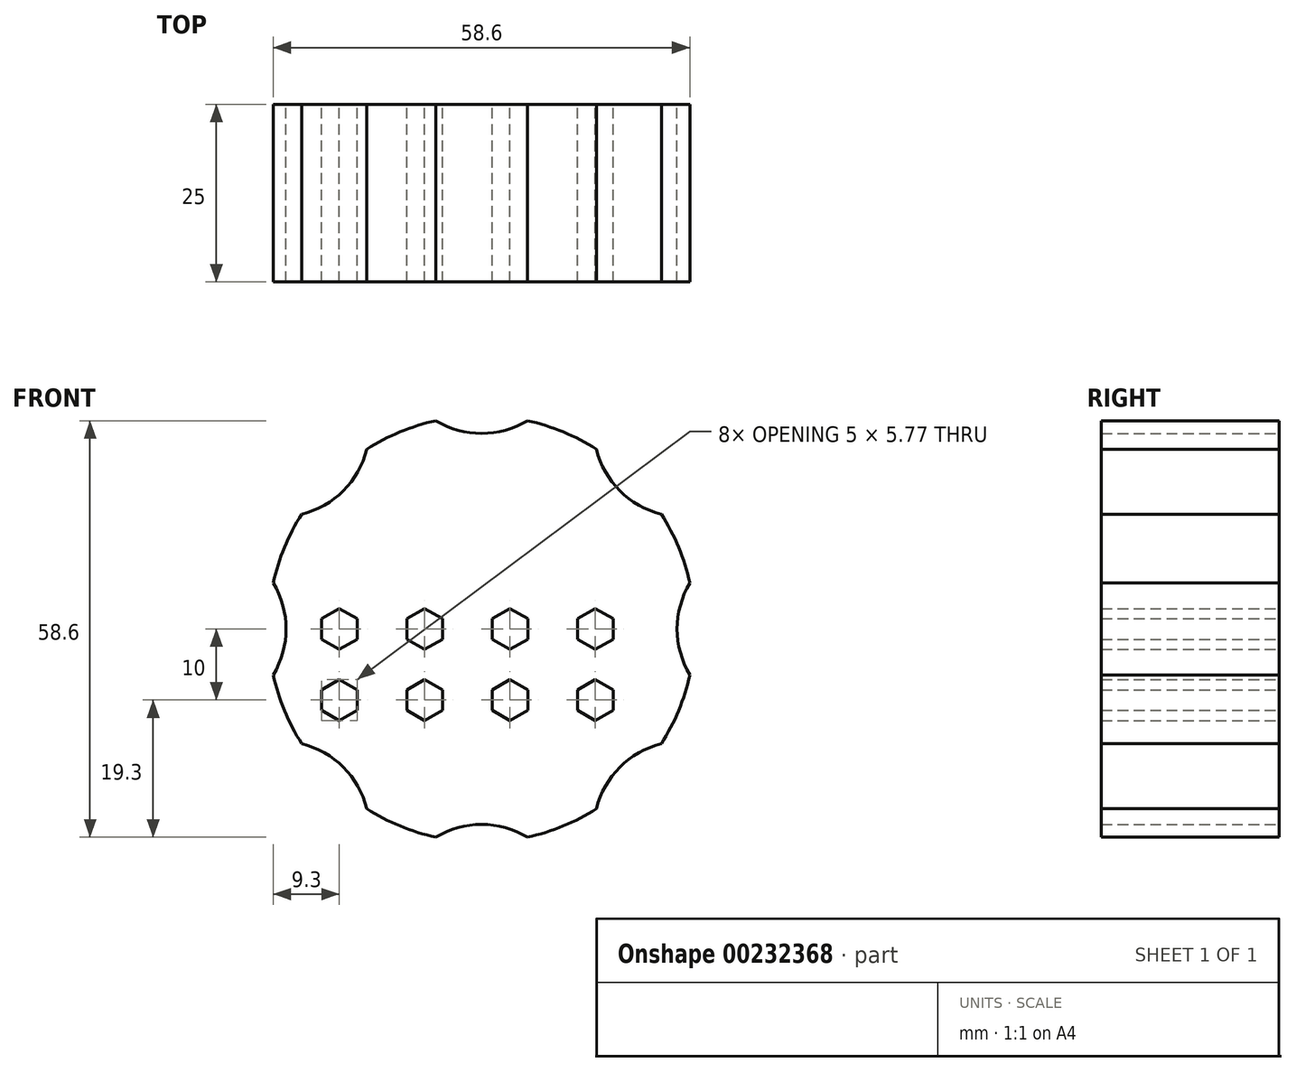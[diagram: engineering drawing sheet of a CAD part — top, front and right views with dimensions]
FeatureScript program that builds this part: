
annotation { "Feature Type Name" : "Feature", "Feature Type Description" : "" }
export const myFeature = defineFeature(function(context is Context, id is Id, definition is map)
    precondition{}
    {
        {
            var Q0;
            Q0=qCreatedBy(makeId("Front.planeOp"),FACE);
            var sketch = newSketch(context, id + "F0", { "sketchPlane" : qUnion([Q0])});
            skArc(sketch, "E0", {"start": v(29.3, 6.46) * mm, "mid": v(27.72, 11.48) * mm, "end": v(25.28, 16.15) * mm});
            skLineSegment(sketch, "E1", {"start": v(-41.86, -10) * mm, "end": v(18.85, -10) * mm, "construction": true});
            skLineSegment(sketch, "E2", {"start": v(-20, -35.68) * mm, "end": v(-20, 9.52) * mm, "construction": true});
            skLineSegment(sketch, "E3", {"start": v(-42.7, 5) * mm, "end": v(18.85, 5) * mm, "construction": true});
            skCircle(sketch, "E4.cCircle", {"center": v(-20, -10) * mm, "radius": 2.5 * mm, "construction": true});
            skLineSegment(sketch, "E4.0", {"start": v(-17.5, -11.44) * mm, "end": v(-20, -12.89) * mm});
            skLineSegment(sketch, "E4.1", {"start": v(-20, -12.89) * mm, "end": v(-22.5, -11.44) * mm});
            skLineSegment(sketch, "E4.2", {"start": v(-22.5, -11.44) * mm, "end": v(-22.5, -8.56) * mm});
            skLineSegment(sketch, "E4.3", {"start": v(-22.5, -8.56) * mm, "end": v(-20, -7.11) * mm});
            skLineSegment(sketch, "E4.4", {"start": v(-20, -7.11) * mm, "end": v(-17.5, -8.56) * mm});
            skLineSegment(sketch, "E4.5", {"start": v(-17.5, -8.56) * mm, "end": v(-17.5, -11.44) * mm});
            skPoint(sketch, "E4.0.midPoint", {"position": v(-18.75, -12.17) * mm});
            skLineSegment(sketch, "E5", {"start": v(40, 21.36) * mm, "end": v(40, -23.63) * mm, "construction": true});
            skArc(sketch, "E6", {"start": v(29.3, 6.46) * mm, "mid": v(27.5, 0) * mm, "end": v(29.3, -6.46) * mm});
            skLineSegment(sketch, "E7.0.1.0", {"start": v(-17.5, -1.44) * mm, "end": v(-20, -2.89) * mm});
            skLineSegment(sketch, "E7.0.1.1", {"start": v(-17.5, 1.44) * mm, "end": v(-17.5, -1.44) * mm});
            skCircle(sketch, "E7.0.1.2", {"center": v(-20, 0) * mm, "radius": 2.5 * mm, "construction": true});
            skLineSegment(sketch, "E7.0.1.3", {"start": v(-20, 2.89) * mm, "end": v(-17.5, 1.44) * mm});
            skLineSegment(sketch, "E7.0.1.4", {"start": v(-22.5, 1.44) * mm, "end": v(-20, 2.89) * mm});
            skLineSegment(sketch, "E7.0.1.5", {"start": v(-22.5, -1.44) * mm, "end": v(-22.5, 1.44) * mm});
            skLineSegment(sketch, "E7.0.1.6", {"start": v(-20, -2.89) * mm, "end": v(-22.5, -1.44) * mm});
            skLineSegment(sketch, "E7.1.0.0", {"start": v(-5.5, -11.44) * mm, "end": v(-8, -12.89) * mm});
            skLineSegment(sketch, "E7.1.0.1", {"start": v(-5.5, -8.56) * mm, "end": v(-5.5, -11.44) * mm});
            skCircle(sketch, "E7.1.0.2", {"center": v(-8, -10) * mm, "radius": 2.5 * mm, "construction": true});
            skLineSegment(sketch, "E7.1.0.3", {"start": v(-8, -7.11) * mm, "end": v(-5.5, -8.56) * mm});
            skLineSegment(sketch, "E7.1.0.4", {"start": v(-10.5, -8.56) * mm, "end": v(-8, -7.11) * mm});
            skLineSegment(sketch, "E7.1.0.5", {"start": v(-10.5, -11.44) * mm, "end": v(-10.5, -8.56) * mm});
            skLineSegment(sketch, "E7.1.0.6", {"start": v(-8, -12.89) * mm, "end": v(-10.5, -11.44) * mm});
            skLineSegment(sketch, "E7.1.1.0", {"start": v(-5.5, -1.44) * mm, "end": v(-8, -2.89) * mm});
            skLineSegment(sketch, "E7.1.1.1", {"start": v(-5.5, 1.44) * mm, "end": v(-5.5, -1.44) * mm});
            skCircle(sketch, "E7.1.1.2", {"center": v(-8, 0) * mm, "radius": 2.5 * mm, "construction": true});
            skLineSegment(sketch, "E7.1.1.3", {"start": v(-8, 2.89) * mm, "end": v(-5.5, 1.44) * mm});
            skLineSegment(sketch, "E7.1.1.4", {"start": v(-10.5, 1.44) * mm, "end": v(-8, 2.89) * mm});
            skLineSegment(sketch, "E7.1.1.5", {"start": v(-10.5, -1.44) * mm, "end": v(-10.5, 1.44) * mm});
            skLineSegment(sketch, "E7.1.1.6", {"start": v(-8, -2.89) * mm, "end": v(-10.5, -1.44) * mm});
            skLineSegment(sketch, "E7.2.0.0", {"start": v(6.5, -11.44) * mm, "end": v(4, -12.89) * mm});
            skLineSegment(sketch, "E7.2.0.1", {"start": v(6.5, -8.56) * mm, "end": v(6.5, -11.44) * mm});
            skCircle(sketch, "E7.2.0.2", {"center": v(4, -10) * mm, "radius": 2.5 * mm, "construction": true});
            skLineSegment(sketch, "E7.2.0.3", {"start": v(4, -7.11) * mm, "end": v(6.5, -8.56) * mm});
            skLineSegment(sketch, "E7.2.0.4", {"start": v(1.5, -8.56) * mm, "end": v(4, -7.11) * mm});
            skLineSegment(sketch, "E7.2.0.5", {"start": v(1.5, -11.44) * mm, "end": v(1.5, -8.56) * mm});
            skLineSegment(sketch, "E7.2.0.6", {"start": v(4, -12.89) * mm, "end": v(1.5, -11.44) * mm});
            skLineSegment(sketch, "E7.2.1.0", {"start": v(6.5, -1.44) * mm, "end": v(4, -2.89) * mm});
            skLineSegment(sketch, "E7.2.1.1", {"start": v(6.5, 1.44) * mm, "end": v(6.5, -1.44) * mm});
            skCircle(sketch, "E7.2.1.2", {"center": v(4, 0) * mm, "radius": 2.5 * mm, "construction": true});
            skLineSegment(sketch, "E7.2.1.3", {"start": v(4, 2.89) * mm, "end": v(6.5, 1.44) * mm});
            skLineSegment(sketch, "E7.2.1.4", {"start": v(1.5, 1.44) * mm, "end": v(4, 2.89) * mm});
            skLineSegment(sketch, "E7.2.1.5", {"start": v(1.5, -1.44) * mm, "end": v(1.5, 1.44) * mm});
            skLineSegment(sketch, "E7.2.1.6", {"start": v(4, -2.89) * mm, "end": v(1.5, -1.44) * mm});
            skLineSegment(sketch, "E7.3.0.0", {"start": v(18.5, -11.44) * mm, "end": v(16, -12.89) * mm});
            skLineSegment(sketch, "E7.3.0.1", {"start": v(18.5, -8.56) * mm, "end": v(18.5, -11.44) * mm});
            skCircle(sketch, "E7.3.0.2", {"center": v(16, -10) * mm, "radius": 2.5 * mm, "construction": true});
            skLineSegment(sketch, "E7.3.0.3", {"start": v(16, -7.11) * mm, "end": v(18.5, -8.56) * mm});
            skLineSegment(sketch, "E7.3.0.4", {"start": v(13.5, -8.56) * mm, "end": v(16, -7.11) * mm});
            skLineSegment(sketch, "E7.3.0.5", {"start": v(13.5, -11.44) * mm, "end": v(13.5, -8.56) * mm});
            skLineSegment(sketch, "E7.3.0.6", {"start": v(16, -12.89) * mm, "end": v(13.5, -11.44) * mm});
            skLineSegment(sketch, "E7.3.1.0", {"start": v(18.5, -1.44) * mm, "end": v(16, -2.89) * mm});
            skLineSegment(sketch, "E7.3.1.1", {"start": v(18.5, 1.44) * mm, "end": v(18.5, -1.44) * mm});
            skCircle(sketch, "E7.3.1.2", {"center": v(16, 0) * mm, "radius": 2.5 * mm, "construction": true});
            skLineSegment(sketch, "E7.3.1.3", {"start": v(16, 2.89) * mm, "end": v(18.5, 1.44) * mm});
            skLineSegment(sketch, "E7.3.1.4", {"start": v(13.5, 1.44) * mm, "end": v(16, 2.89) * mm});
            skLineSegment(sketch, "E7.3.1.5", {"start": v(13.5, -1.44) * mm, "end": v(13.5, 1.44) * mm});
            skLineSegment(sketch, "E7.3.1.6", {"start": v(16, -2.89) * mm, "end": v(13.5, -1.44) * mm});
            skLineSegment(sketch, "E7.direction1", {"start": v(-20, -12.89) * mm, "end": v(-8, -12.89) * mm, "construction": true});
            skLineSegment(sketch, "E7.direction2", {"start": v(-20, -12.89) * mm, "end": v(-20, -2.89) * mm, "construction": true});
            skArc(sketch, "E8.1.0", {"start": v(16.15, 25.28) * mm, "mid": v(19.45, 19.45) * mm, "end": v(25.28, 16.15) * mm});
            skArc(sketch, "E8.2.0", {"start": v(-6.46, 29.3) * mm, "mid": v(0, 27.5) * mm, "end": v(6.46, 29.3) * mm});
            skArc(sketch, "E8.3.0", {"start": v(-25.28, 16.15) * mm, "mid": v(-19.45, 19.45) * mm, "end": v(-16.15, 25.28) * mm});
            skArc(sketch, "E8.4.0", {"start": v(-29.3, -6.46) * mm, "mid": v(-27.5, 0) * mm, "end": v(-29.3, 6.46) * mm});
            skArc(sketch, "E8.5.0", {"start": v(-16.15, -25.28) * mm, "mid": v(-19.45, -19.45) * mm, "end": v(-25.28, -16.15) * mm});
            skArc(sketch, "E8.6.0", {"start": v(6.46, -29.3) * mm, "mid": v(0, -27.5) * mm, "end": v(-6.46, -29.3) * mm});
            skArc(sketch, "E8.7.0", {"start": v(25.28, -16.15) * mm, "mid": v(19.45, -19.45) * mm, "end": v(16.15, -25.28) * mm});
            skArc(sketch, "E9.trimOffspring", {"start": v(25.28, -16.15) * mm, "mid": v(27.72, -11.48) * mm, "end": v(29.3, -6.46) * mm});
            skArc(sketch, "E10.trimOffspring", {"start": v(6.46, -29.3) * mm, "mid": v(11.48, -27.72) * mm, "end": v(16.15, -25.28) * mm});
            skArc(sketch, "E11.trimOffspring", {"start": v(-16.15, -25.28) * mm, "mid": v(-11.48, -27.72) * mm, "end": v(-6.46, -29.3) * mm});
            skArc(sketch, "E12.trimOffspring", {"start": v(-29.3, -6.46) * mm, "mid": v(-27.72, -11.48) * mm, "end": v(-25.28, -16.15) * mm});
            skArc(sketch, "E13.trimOffspring", {"start": v(-25.28, 16.15) * mm, "mid": v(-27.72, 11.48) * mm, "end": v(-29.3, 6.46) * mm});
            skArc(sketch, "E14.trimOffspring", {"start": v(-6.46, 29.3) * mm, "mid": v(-11.48, 27.72) * mm, "end": v(-16.15, 25.28) * mm});
            skArc(sketch, "E15.trimOffspring", {"start": v(16.15, 25.28) * mm, "mid": v(11.48, 27.72) * mm, "end": v(6.46, 29.3) * mm});
            skSolve(sketch);
        }
        {
            var Q0;
            Q0=makeQuery(id+"F0.imprint","IMPRINT",FACE,{"disambiguationData":[TD([[makeQuery(id+"F0.imprint","IMPRINT",EDGE,{"derivedFrom":sQuery(id+"F0.wireOp",EDGE,"E0")}),1.0]])]});
            extrude(context, id + "F1", {"entities" : qUnion([Q0]), "depth" : 25 * mm});
        }
    });
